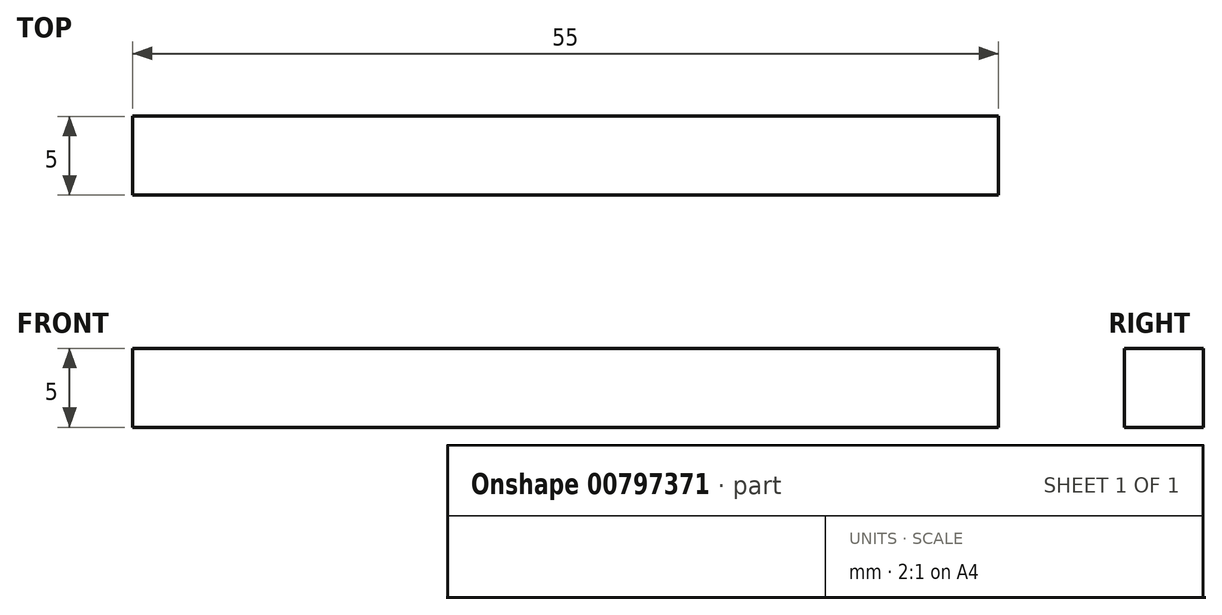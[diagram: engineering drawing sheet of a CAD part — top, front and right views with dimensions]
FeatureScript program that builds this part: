
annotation { "Feature Type Name" : "Feature", "Feature Type Description" : "" }
export const myFeature = defineFeature(function(context is Context, id is Id, definition is map)
    precondition{}
    {
        {
            var Q0;
            Q0=qCreatedBy(makeId("Top.planeOp"),FACE);
            var sketch = newSketch(context, id + "F0", { "sketchPlane" : qUnion([Q0])});
            skLineSegment(sketch, "E0.bottom", {"start": v(-27.92, 14.2) * mm, "end": v(27.08, 14.2) * mm});
            skLineSegment(sketch, "E0.top", {"start": v(-27.92, 9.2) * mm, "end": v(27.08, 9.2) * mm});
            skLineSegment(sketch, "E0.left", {"start": v(-27.92, 14.2) * mm, "end": v(-27.92, 9.2) * mm});
            skLineSegment(sketch, "E0.right", {"start": v(27.08, 14.2) * mm, "end": v(27.08, 9.2) * mm});
            skSolve(sketch);
        }
        {
            var Q0;
            Q0 = qSketchRegion(id + "F0", true);
            extrude(context, id + "F1", {"entities" : qUnion([Q0]), "depth" : 5 * mm, "offsetDistance" : 25.4 * mm});
        }
    });
